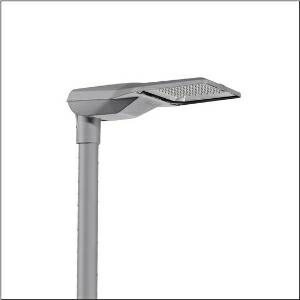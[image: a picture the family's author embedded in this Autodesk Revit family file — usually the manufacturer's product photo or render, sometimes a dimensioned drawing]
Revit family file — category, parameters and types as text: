
# Revit family: streetlight_sl_21_iq_midi___pc-r_5xe3g41g08mb_0911
name_source: partatom
category: Lighting Fixtures
units: mm (PartAtom-declared; Revit-internal decimal feet)

## family parameters
Cut with Voids When Loaded = No
Host = Face
Light Source = No
Part Type = Normal
Room Calculation Point = No
Round Connector Dimension = Use Diameter
Shared = No

## types (1)
- --- (1 x LED, 19370 lm, 146.7 W, 4000K)
    Apparent Load = 147 VA
    CIE Flux Codes = 38 78 98 100 100
    Color Rendering = 70
    Color Temperature = 4000K
    Default Elevation = 1800 mm
    Description = Streetlight SL 21 iQ midi, mast luminaire, primary light control with lens, of PMMA, primary optical cover: cover, of toughened safety glass, transparent, light distribution: PC-R, light emission: direct distribution, primary light characteristic: asymmetric, right, installation type: post-top, side-entry, LED, High Power LED, rated luminous flux: 19.370lm, luminous efficacy: 132lm/W, light colour: 740, colour temperature: 4000K, control gear: iQ Street-Remote, control: Street-Remote, Auto-Match, Temp-Guard, Lumen-Switch, Night-Set, Smart-Wire, Light-Fading, Desk-Remote (wireless, voltage-free reading and setting of iQ features in the workshop via application-optimized NFC function/RFID function), optimised constant luminous flux control (CLO 2.0), pre-setting: linear dimming characteristic, mains connection: 230..240V, AC, 50/60Hz, start of lifetime: 147W, end of service life: 161W, reduction: 62W, luminaire housing, of diecast aluminium, powder-coated, SITECO metallic grey (DB 702S), corrosivity category C5 high according to DIN EN ISO 12944, please order mast flange separately, inclination adjustable: 0°, 5°, 10°, 15°, sealing non-destructively replaceable, multi-level sealing system, length: 644mm, width: 335mm, height: 110mm, mast flange for spigot size: 42mm (side-entry): 5XC10008XM4, 60/48mm (side-entry/post-top): 5XC10108XM2, 76/60mm (side-entry/post-top): 5XC10108XM1, mounting height: 4..8m, protection rating (complete): IP66, insulation class (complete): insulation class II (safety insulation), certification: CE, ENEC, ENEC+, VDE, impact resistance: IK10, permissible operating ambient temperature for outdoor applications: -40..+50°C, standard-compliant lighting for roads and squares, packaging unit: 1 piece

Light Distribution: PC-R
    Height = 111 mm
    Lamp = 1 x LED
    Lamp Light Flux = 19370 lm
    Lamp Power = 146.7 W
    Lamp count = 1
    Length = 644 mm
    Luminous efficacy = 132 lm/W
    Manufacturer = Siteco
    ModVariant = No
    Model = 5XE3G41G08MB
    Number of Poles = 1
    OnlyDefault = Yes
    Power Factor = 1
    Product Name = Streetlight SL 21 iQ midi | PC-R
    Product group = mast luminaire | pylon top
    ProductGroupID = 6100
    Protection Class = Protection class II
    Protection Degree = IP 66
    RLX_Detail_Level = 1
    RLX_Emergency_Light_Flux = 0 lm
    RLX_Emergency_Type = 0
    RLX_Emergency_Type_DB = No
    RlxData = <blob elided: 29489 chars, md5=2803f5e0>
    Socket = socket
    Standby Power = 0 W
    System Light Flux = 19370 lm
    System Power = 147 W
    Type Comments = factory setting: luminous flux: 100 % | dim-lin: 254 | 753 mA
    Type Image = l_1004298.jpg
    URL = http://relux.com
    VarID = @adj_071699
    Voltage = 0 V
    Weight = 0.00 kg
    Width = 336 mm

## geometry (parser evidence)
native form markers: Blend x4, Sweep x10
no freeform markers — native parametric forms only
